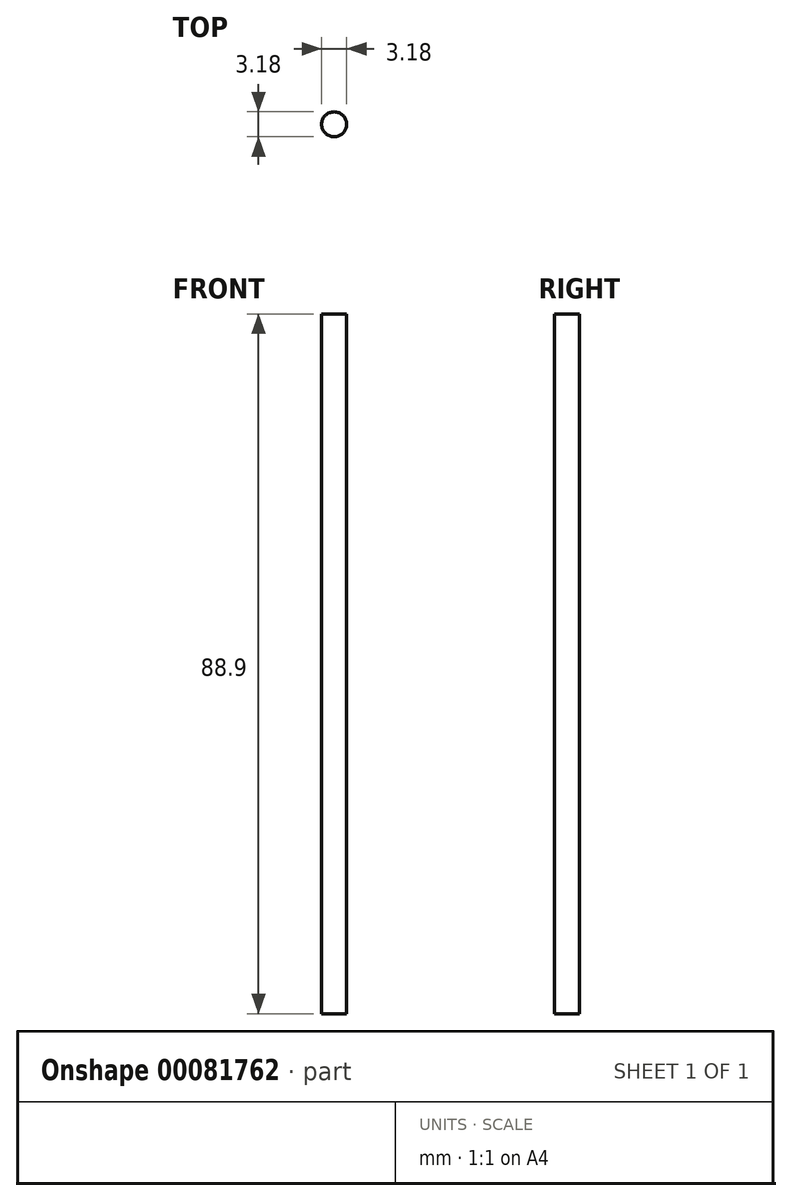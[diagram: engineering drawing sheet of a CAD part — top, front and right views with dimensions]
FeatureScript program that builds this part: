
annotation { "Feature Type Name" : "Feature", "Feature Type Description" : "" }
export const myFeature = defineFeature(function(context is Context, id is Id, definition is map)
    precondition{}
    {
        {
            var Q0;
            Q0=qCreatedBy(makeId("Top.planeOp"),FACE);
            var sketch = newSketch(context, id + "F0", { "sketchPlane" : qUnion([Q0])});
            skCircle(sketch, "E0", {"center": v(0, 0) * mm, "radius": 1.59 * mm});
            skSolve(sketch);
        }
        {
            var Q0;
            Q0 = qSketchRegion(id + "F0", true);
            extrude(context, id + "F1", {"entities" : qUnion([Q0]), "depth" : 88.9 * mm});
        }
    });
